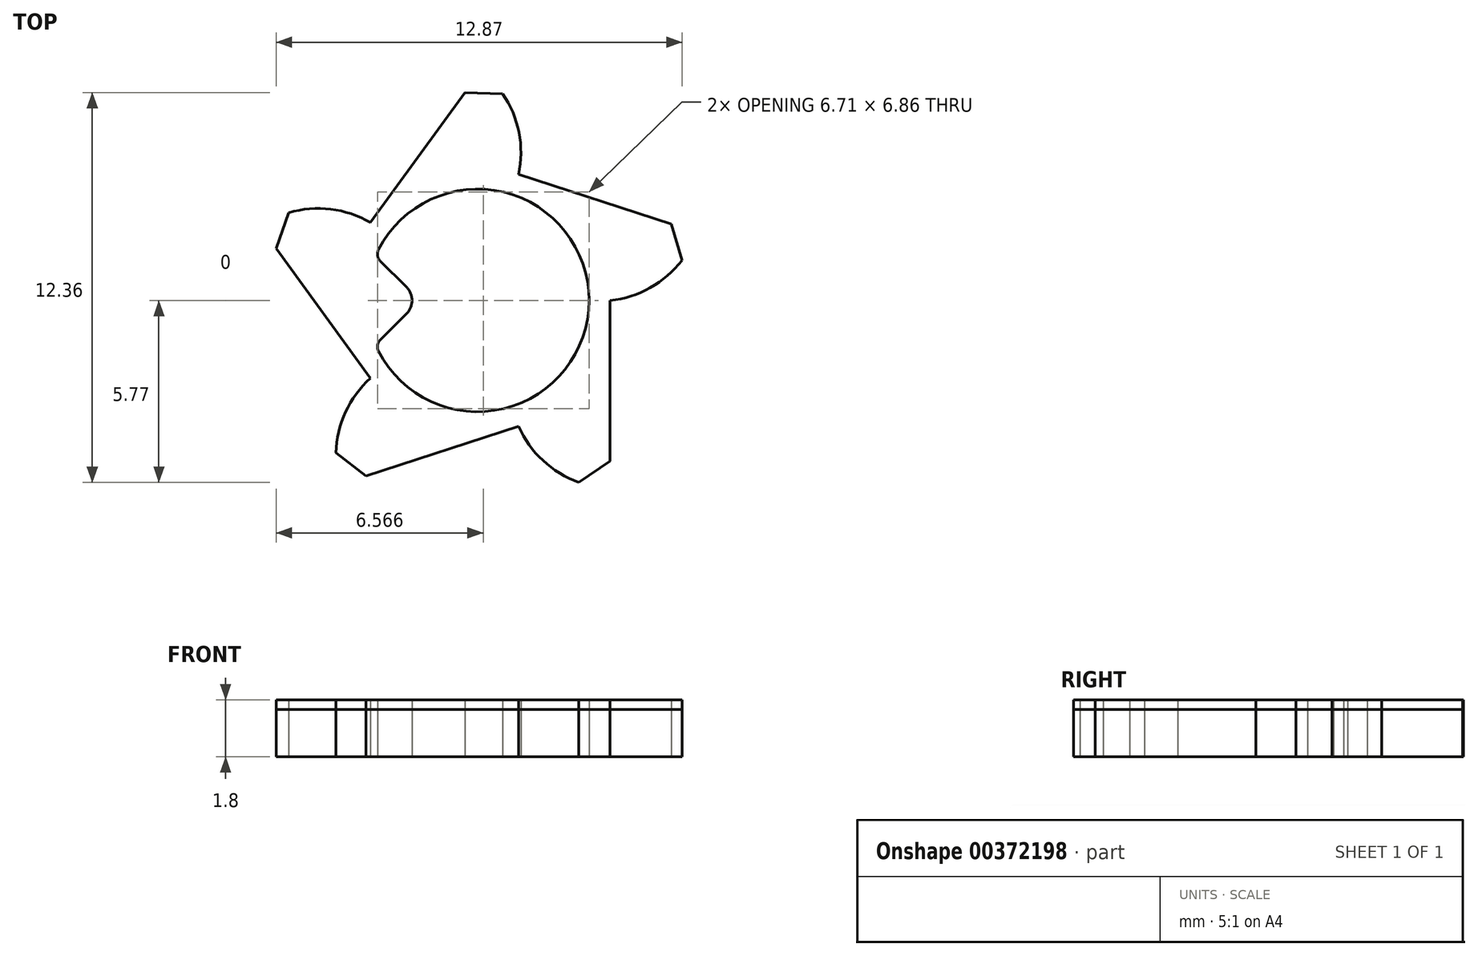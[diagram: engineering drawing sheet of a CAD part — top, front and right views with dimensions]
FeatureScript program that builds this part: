
annotation { "Feature Type Name" : "Feature", "Feature Type Description" : "" }
export const myFeature = defineFeature(function(context is Context, id is Id, definition is map)
    precondition{}
    {
        {
            var Q0;
            Q0=qCreatedBy(makeId("Top.planeOp"),FACE);
            var sketch = newSketch(context, id + "F0", { "sketchPlane" : qUnion([Q0])});
            skCircle(sketch, "E0", {"center": v(0, 0) * mm, "radius": 1.4 * mm, "construction": true});
            skCircle(sketch, "E1", {"center": v(0, 0) * mm, "radius": 1.65 * mm, "construction": true});
            skCircle(sketch, "E2", {"center": v(0, 0) * mm, "radius": 2.2 * mm, "construction": true});
            skArc(sketch, "E3", {"start": v(-1.05, -0.53) * mm, "mid": v(1.18, 0) * mm, "end": v(-1.05, 0.53) * mm});
            skLineSegment(sketch, "E4", {"start": v(0, 0) * mm, "end": v(1.4, 0) * mm, "construction": true});
            skLineSegment(sketch, "E5", {"start": v(0, 0) * mm, "end": v(0.43, -1.33) * mm, "construction": true});
            skLineSegment(sketch, "E6", {"start": v(0, 0) * mm, "end": v(-1.13, -0.82) * mm, "construction": true});
            skLineSegment(sketch, "E7", {"start": v(0, 0) * mm, "end": v(-1.13, 0.82) * mm, "construction": true});
            skLineSegment(sketch, "E8", {"start": v(0, 0) * mm, "end": v(0.43, 1.33) * mm, "construction": true});
            skLineSegment(sketch, "E9", {"start": v(1.4, 0) * mm, "end": v(1.4, -1.7) * mm});
            skLineSegment(sketch, "E10", {"start": v(1.4, -1.7) * mm, "end": v(1.07, -1.92) * mm});
            skLineSegment(sketch, "E11", {"start": v(0.43, -1.33) * mm, "end": v(-1.18, -1.86) * mm});
            skLineSegment(sketch, "E12", {"start": v(-1.18, -1.86) * mm, "end": v(-1.5, -1.61) * mm});
            skLineSegment(sketch, "E13", {"start": v(-1.13, -0.82) * mm, "end": v(-2.13, 0.55) * mm});
            skLineSegment(sketch, "E14", {"start": v(-2.13, 0.55) * mm, "end": v(-2, 0.93) * mm});
            skLineSegment(sketch, "E15", {"start": v(-1.13, 0.82) * mm, "end": v(-0.14, 2.2) * mm});
            skLineSegment(sketch, "E16", {"start": v(-0.14, 2.2) * mm, "end": v(0.26, 2.18) * mm});
            skLineSegment(sketch, "E17", {"start": v(0.43, 1.33) * mm, "end": v(2.05, 0.8) * mm});
            skLineSegment(sketch, "E18", {"start": v(2.05, 0.8) * mm, "end": v(2.16, 0.42) * mm});
            skArc(sketch, "E19", {"start": v(0.43, -1.33) * mm, "mid": v(0.7, -1.7) * mm, "end": v(1.07, -1.92) * mm});
            skPoint(sketch, "E19.third.point", {"position": v(0.36, -1.12) * mm});
            skArc(sketch, "E20", {"start": v(-1.13, -0.82) * mm, "mid": v(-1.4, -1.18) * mm, "end": v(-1.5, -1.61) * mm});
            skPoint(sketch, "E20.third.point", {"position": v(-0.95, -0.7) * mm});
            skPoint(sketch, "E21.third.point", {"position": v(-0.95, 0.7) * mm});
            skPoint(sketch, "E22.third.point", {"position": v(0.36, 1.12) * mm});
            skArc(sketch, "E23", {"start": v(1.4, 0) * mm, "mid": v(1.82, 0.13) * mm, "end": v(2.16, 0.42) * mm});
            skPoint(sketch, "E23.third.point", {"position": v(1.18, 0) * mm});
            skArc(sketch, "E24.trimOffspring", {"start": v(0.43, 1.33) * mm, "mid": v(0.44, 1.78) * mm, "end": v(0.26, 2.18) * mm});
            skLineSegment(sketch, "E25", {"start": v(0, 0) * mm, "end": v(-0.61, 0) * mm, "construction": true});
            skLineSegment(sketch, "E26", {"start": v(-0.75, 0.14) * mm, "end": v(-1.03, 0.42) * mm});
            skLineSegment(sketch, "E27", {"start": v(-0.75, -0.14) * mm, "end": v(-1.03, -0.42) * mm});
            skPoint(sketch, "E28.visualSharp", {"position": v(-0.61, 0) * mm});
            skArc(sketch, "E28.filletArc", {"start": v(-0.75, -0.14) * mm, "mid": v(-0.7, 0) * mm, "end": v(-0.75, 0.14) * mm});
            skPoint(sketch, "E29.visualSharp", {"position": v(-1.08, 0.47) * mm});
            skArc(sketch, "E29.filletArc", {"start": v(-1.05, 0.53) * mm, "mid": v(-1.06, 0.47) * mm, "end": v(-1.03, 0.42) * mm});
            skPoint(sketch, "E30.visualSharp", {"position": v(-1.08, -0.47) * mm});
            skArc(sketch, "E30.filletArc", {"start": v(-1.03, -0.42) * mm, "mid": v(-1.06, -0.47) * mm, "end": v(-1.05, -0.53) * mm});
            skLineSegment(sketch, "E31", {"start": v(0, 0) * mm, "end": v(-2.17, 0.34) * mm, "construction": true});
            skArc(sketch, "E32", {"start": v(-1.13, 0.82) * mm, "mid": v(-1.55, 0.96) * mm, "end": v(-2, 0.93) * mm});
            skSolve(sketch);
        }
        {
            var Q0;
            Q0=makeQuery(id+"F0.imprint","IMPRINT",FACE,{"disambiguationData":[TD([[makeQuery(id+"F0.imprint","IMPRINT",EDGE,{"derivedFrom":sQuery(id+"F0.wireOp",EDGE,"E3")}),-1.0]])]});
            extrude(context, id + "F1", {"entities" : qUnion([Q0]), "depth" : 0.5 * mm});
        }
        {
            var Q0;
            Q0=makeQuery(id+"F0.imprint","IMPRINT",FACE,{"disambiguationData":[TD([[makeQuery(id+"F0.imprint","IMPRINT",EDGE,{"derivedFrom":sQuery(id+"F0.wireOp",EDGE,"E3")}),-1.0]])]});
            extrude(context, id + "F2", {"entities" : qUnion([Q0]), "depth" : 0.6 * mm});
        }
        {
            var Q0;
            Q0=makeQuery(id+"F2.opExtrude","SWEPT_BODY",BODY,{"disambiguationData":[OSD([sQuery(id+"F0.wireOp",EDGE,"E3"),sQuery(id+"F0.wireOp",EDGE,"E9"),sQuery(id+"F0.wireOp",EDGE,"E10"),sQuery(id+"F0.wireOp",EDGE,"E11"),sQuery(id+"F0.wireOp",EDGE,"E12"),sQuery(id+"F0.wireOp",EDGE,"E13"),sQuery(id+"F0.wireOp",EDGE,"E14"),sQuery(id+"F0.wireOp",EDGE,"E15"),sQuery(id+"F0.wireOp",EDGE,"E16"),sQuery(id+"F0.wireOp",EDGE,"E17"),sQuery(id+"F0.wireOp",EDGE,"E18"),sQuery(id+"F0.wireOp",EDGE,"E19"),sQuery(id+"F0.wireOp",EDGE,"E20"),sQuery(id+"F0.wireOp",EDGE,"E23"),sQuery(id+"F0.wireOp",EDGE,"E24.trimOffspring"),sQuery(id+"F0.wireOp",EDGE,"E26"),sQuery(id+"F0.wireOp",EDGE,"E27"),sQuery(id+"F0.wireOp",EDGE,"E28.filletArc"),sQuery(id+"F0.wireOp",EDGE,"E29.filletArc"),sQuery(id+"F0.wireOp",EDGE,"E30.filletArc"),sQuery(id+"F0.wireOp",EDGE,"E32")])]});
            var Q1;
            Q1=makeQuery(id+"F1.opExtrude","SWEPT_BODY",BODY,{"disambiguationData":[OSD([sQuery(id+"F0.wireOp",EDGE,"E3"),sQuery(id+"F0.wireOp",EDGE,"E9"),sQuery(id+"F0.wireOp",EDGE,"E10"),sQuery(id+"F0.wireOp",EDGE,"E11"),sQuery(id+"F0.wireOp",EDGE,"E12"),sQuery(id+"F0.wireOp",EDGE,"E13"),sQuery(id+"F0.wireOp",EDGE,"E14"),sQuery(id+"F0.wireOp",EDGE,"E15"),sQuery(id+"F0.wireOp",EDGE,"E16"),sQuery(id+"F0.wireOp",EDGE,"E17"),sQuery(id+"F0.wireOp",EDGE,"E18"),sQuery(id+"F0.wireOp",EDGE,"E19"),sQuery(id+"F0.wireOp",EDGE,"E20"),sQuery(id+"F0.wireOp",EDGE,"E23"),sQuery(id+"F0.wireOp",EDGE,"E24.trimOffspring"),sQuery(id+"F0.wireOp",EDGE,"E26"),sQuery(id+"F0.wireOp",EDGE,"E27"),sQuery(id+"F0.wireOp",EDGE,"E28.filletArc"),sQuery(id+"F0.wireOp",EDGE,"E29.filletArc"),sQuery(id+"F0.wireOp",EDGE,"E30.filletArc"),sQuery(id+"F0.wireOp",EDGE,"E32")])]});
            var Q2;
            Q2=qCreatedBy(makeId("Origin.pointOp"),VERTEX);
            transform(context, id + "F3", {"entities" : qUnion([Q0, Q1]), "transformType" : TransformType.SCALE_UNIFORMLY, "scale" : 3, "makeCopy" : false, "scalePoint" : qUnion([Q2])});
        }
    });
